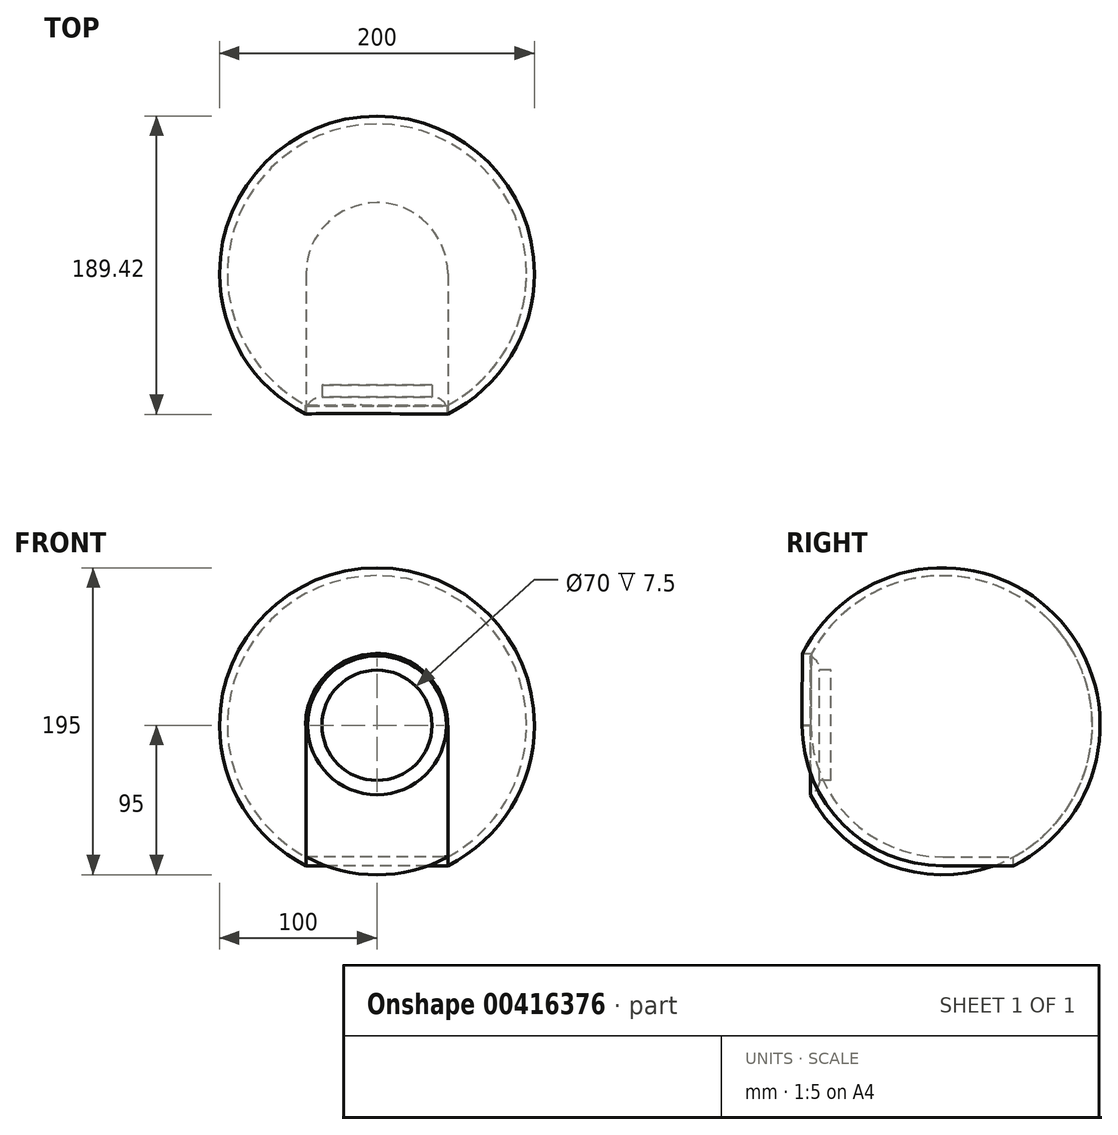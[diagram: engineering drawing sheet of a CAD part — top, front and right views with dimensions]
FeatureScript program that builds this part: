
annotation { "Feature Type Name" : "Feature", "Feature Type Description" : "" }
export const myFeature = defineFeature(function(context is Context, id is Id, definition is map)
    precondition{}
    {
        {
            assignVariable(context, id + "F0", {"name" : "bodyDiam", "anyValue" : 200});
        }
        {
            assignVariable(context, id + "F1", {"name" : "shellThickness", "anyValue" : 5});
        }
        {
            var Q0;
            Q0=qCreatedBy(makeId("Front.planeOp"),FACE);
            var sketch = newSketch(context, id + "F2", { "sketchPlane" : qUnion([Q0])});
            skCircle(sketch, "E0", {"center": v(0, 0) * mm, "radius": 100 * mm});
            skCircle(sketch, "E1", {"center": v(-0.22, 0.55) * mm, "radius": 45 * mm});
            skLineSegment(sketch, "E2", {"start": v(0, 0) * mm, "end": v(100, 0) * mm});
            skLineSegment(sketch, "E3", {"start": v(0, 0) * mm, "end": v(-100, 0) * mm});
            skCircle(sketch, "E4", {"center": v(0, 0) * mm, "radius": 95 * mm});
            skSolve(sketch);
        }
        {
            var Q0;
            Q0=qCreatedBy(makeId("Top.planeOp"),FACE);
            var sketch = newSketch(context, id + "F3", { "sketchPlane" : qUnion([Q0])});
            skCircle(sketch, "E5", {"center": v(0, 0) * mm, "radius": 45 * mm});
            skLineSegment(sketch, "E6", {"start": v(-45, 0) * mm, "end": v(-45, -100) * mm});
            skLineSegment(sketch, "E7", {"start": v(45, 0) * mm, "end": v(45, -100) * mm});
            skLineSegment(sketch, "E8", {"start": v(45, -100) * mm, "end": v(-45, -100) * mm});
            skSolve(sketch);
        }
        {
            var Q0;
            Q0=qCreatedBy(makeId("Right.planeOp"),FACE);
            var sketch = newSketch(context, id + "F4", { "sketchPlane" : qUnion([Q0])});
            skLineSegment(sketch, "E9", {"start": v(0, 0) * mm, "end": v(-95, 0) * mm});
            skCircle(sketch, "E10", {"center": v(0, 0) * mm, "radius": 95 * mm});
            skLineSegment(sketch, "E11", {"start": v(-88.32, 35) * mm, "end": v(-88.32, -35) * mm});
            skCircle(sketch, "E12", {"center": v(-88.32, -35) * mm, "radius": 10 * mm});
            skCircle(sketch, "E13", {"center": v(-88.32, 35) * mm, "radius": 10 * mm});
            skLineSegment(sketch, "E14", {"start": v(-78.32, 35) * mm, "end": v(-78.32, -35) * mm});
            skSolve(sketch);
        }
        {
            var Q0;
            {var subQ0=sQuery(id+"F2.wireOp",EDGE,"E2");var subQ1=sQuery(id+"F2.wireOp",EDGE,"E0");var subQ2=makeQuery(id+"F2.imprint","INTERSECT",VERTEX,{"derivedFrom":[subQ1,subQ0]});Q0=makeQuery(id+"F2.imprint","IMPRINT",FACE,{"disambiguationData":[TD([[makeQuery(id+"F2.imprint","IMPRINT",EDGE,{"disambiguationData":[TD([[subQ2,-1.0]])],"derivedFrom":subQ1}),1.0]])]});}
            var Q1;
            {var subQ0=sQuery(id+"F2.wireOp",EDGE,"E2");var subQ1=sQuery(id+"F2.wireOp",EDGE,"E1");var subQ2=makeQuery(id+"F2.imprint","INTERSECT",VERTEX,{"derivedFrom":[subQ1,subQ0]});Q1=makeQuery(id+"F2.imprint","IMPRINT",FACE,{"disambiguationData":[TD([[makeQuery(id+"F2.imprint","IMPRINT",EDGE,{"disambiguationData":[TD([[subQ2,-1.0]])],"derivedFrom":subQ1}),1.0]])]});}
            var Q2;
            {var subQ0=sQuery(id+"F2.wireOp",EDGE,"E2");var subQ1=sQuery(id+"F2.wireOp",EDGE,"E1");var subQ2=makeQuery(id+"F2.imprint","INTERSECT",VERTEX,{"derivedFrom":[subQ1,subQ0]});Q2=makeQuery(id+"F2.imprint","IMPRINT",FACE,{"disambiguationData":[TD([[makeQuery(id+"F2.imprint","IMPRINT",EDGE,{"disambiguationData":[TD([[subQ2,-1.0]])],"derivedFrom":subQ1}),-1.0]])]});}
            var Q3;
            Q3=sQuery(id+"F2.wireOp",EDGE,"E3");
            revolve(context, id + "F5", {"entities" : qUnion([Q0, Q1, Q2]), "axis" : qUnion([Q3]), "revolveType" : RevolveType.FULL});
        }
        {
            var Q0;
            Q0=makeQuery(id+"F5.opRevolve","SWEPT_FACE",FACE,{"disambiguationData":[OSD([sQuery(id+"F2.wireOp",EDGE,"E0")])]});
            var Q1;
            Q1=makeQuery(id+"F5.opRevolve","SWEPT_BODY",BODY,{"disambiguationData":[OSD([sQuery(id+"F2.wireOp",EDGE,"E0"),sQuery(id+"F2.wireOp",EDGE,"E2"),sQuery(id+"F2.wireOp",EDGE,"E3")])]});
            shell(context, id + "F6", {"isHollow" : true, "entities" : qUnion([Q0]), "parts" : qUnion([Q1]), "thickness" : (getVariable(context, 'shellThickness')) * mm});
        }
        {
            var Q0;
            {var subQ0=sQuery(id+"F2.wireOp",EDGE,"E2");var subQ1=sQuery(id+"F2.wireOp",EDGE,"E1");var subQ2=makeQuery(id+"F2.imprint","INTERSECT",VERTEX,{"derivedFrom":[subQ1,subQ0]});Q0=makeQuery(id+"F2.imprint","IMPRINT",FACE,{"disambiguationData":[TD([[makeQuery(id+"F2.imprint","IMPRINT",EDGE,{"disambiguationData":[TD([[subQ2,-1.0]])],"derivedFrom":subQ1}),1.0]])]});}
            extrude(context, id + "F7", {"entities" : qUnion([Q0]), "operationType" : NewBodyOperationType.REMOVE, "depth" : (getVariable(context, 'bodyDiam')) * mm});
        }
        {
            var Q0;
            {var subQ0=sQuery(id+"F3.wireOp",EDGE,"E5");var subQ1=makeQuery(id+"F3.imprint","INTERSECT",VERTEX,{"derivedFrom":[subQ0,sQuery(id+"F3.wireOp",EDGE,"E6")]});Q0=makeQuery(id+"F3.imprint","IMPRINT",FACE,{"disambiguationData":[TD([[makeQuery(id+"F3.imprint","IMPRINT",EDGE,{"disambiguationData":[TD([[subQ1,1.0]])],"derivedFrom":subQ0}),1.0]])]});}
            var Q1;
            {var subQ0=sQuery(id+"F3.wireOp",EDGE,"E6");Q1=makeQuery(id+"F3.imprint","IMPRINT",FACE,{"disambiguationData":[TD([[makeQuery(id+"F3.imprint","IMPRINT",EDGE,{"derivedFrom":subQ0}),1.0]])]});}
            extrude(context, id + "F8", {"entities" : qUnion([Q0, Q1]), "operationType" : NewBodyOperationType.REMOVE, "oppositeDirection" : true, "depth" : (getVariable(context, 'bodyDiam')) * mm});
        }
        {
            var Q0;
            {var subQ0=sQuery(id+"F2.wireOp",EDGE,"E2");var subQ1=sQuery(id+"F2.wireOp",EDGE,"E1");var subQ2=makeQuery(id+"F2.imprint","INTERSECT",VERTEX,{"derivedFrom":[subQ1,subQ0]});Q0=makeQuery(id+"F2.imprint","IMPRINT",FACE,{"disambiguationData":[TD([[makeQuery(id+"F2.imprint","IMPRINT",EDGE,{"disambiguationData":[TD([[subQ2,-1.0]])],"derivedFrom":subQ1}),-1.0]])]});}
            var Q1;
            {var subQ0=sQuery(id+"F2.wireOp",EDGE,"E2");var subQ1=sQuery(id+"F2.wireOp",EDGE,"E1");var subQ2=makeQuery(id+"F2.imprint","INTERSECT",VERTEX,{"derivedFrom":[subQ1,subQ0]});Q1=makeQuery(id+"F2.imprint","IMPRINT",FACE,{"disambiguationData":[TD([[makeQuery(id+"F2.imprint","IMPRINT",EDGE,{"disambiguationData":[TD([[subQ2,-1.0]])],"derivedFrom":subQ1}),1.0]])]});}
            var Q2;
            Q2=sQuery(id+"F2.wireOp",EDGE,"E2");
            revolve(context, id + "F9", {"entities" : qUnion([Q0, Q1]), "axis" : qUnion([Q2]), "revolveType" : RevolveType.FULL});
        }
        {
            var Q0;
            {var subQ0=sQuery(id+"F4.wireOp",EDGE,"E11");var subQ1=sQuery(id+"F4.wireOp",EDGE,"E10");var subQ2=makeQuery(id+"F4.imprint","INTERSECT",VERTEX,{"disambiguationData":[OD(0.0)],"derivedFrom":[subQ1,subQ0]});Q0=makeQuery(id+"F4.imprint","IMPRINT",FACE,{"disambiguationData":[TD([[makeQuery(id+"F4.imprint","IMPRINT",EDGE,{"disambiguationData":[TD([[subQ2,1.0]])],"derivedFrom":subQ1}),1.0]])]});}
            var Q1;
            {var subQ0=sQuery(id+"F4.wireOp",EDGE,"E11");var subQ1=sQuery(id+"F4.wireOp",EDGE,"E10");var subQ2=makeQuery(id+"F4.imprint","INTERSECT",VERTEX,{"disambiguationData":[OD(0.0)],"derivedFrom":[subQ1,subQ0]});Q1=makeQuery(id+"F4.imprint","IMPRINT",FACE,{"disambiguationData":[TD([[makeQuery(id+"F4.imprint","IMPRINT",EDGE,{"disambiguationData":[TD([[subQ2,-1.0]])],"derivedFrom":subQ1}),1.0]])]});}
            var Q2;
            {var subQ0=sQuery(id+"F4.wireOp",EDGE,"E10");var subQ1=sQuery(id+"F4.wireOp",EDGE,"E9");var subQ2=makeQuery(id+"F4.imprint","INTERSECT",VERTEX,{"derivedFrom":[subQ1,subQ0]});Q2=makeQuery(id+"F4.imprint","IMPRINT",FACE,{"disambiguationData":[TD([[makeQuery(id+"F4.imprint","IMPRINT",EDGE,{"disambiguationData":[TD([[subQ2,1.0]])],"derivedFrom":subQ1}),-1.0]])]});}
            var Q3;
            {var subQ0=sQuery(id+"F4.wireOp",EDGE,"E14");var subQ1=sQuery(id+"F4.wireOp",EDGE,"E9");var subQ2=makeQuery(id+"F4.imprint","INTERSECT",VERTEX,{"derivedFrom":[subQ1,subQ0]});Q3=makeQuery(id+"F4.imprint","IMPRINT",FACE,{"disambiguationData":[TD([[makeQuery(id+"F4.imprint","IMPRINT",EDGE,{"disambiguationData":[TD([[subQ2,-1.0]])],"derivedFrom":subQ1}),-1.0]])]});}
            var Q4;
            Q4=sQuery(id+"F4.wireOp",EDGE,"E9");
            revolve(context, id + "F10", {"operationType" : NewBodyOperationType.REMOVE, "entities" : qUnion([Q0, Q1, Q2, Q3]), "axis" : qUnion([Q4]), "revolveType" : RevolveType.FULL, "oppositeDirection" : true});
        }
        {
            var Q0;
            Q0=makeQuery(id+"F10.boolean.opBoolean","COPY",FACE,{"derivedFrom":makeQuery(id+"F10.opRevolve","SWEPT_FACE",FACE,{"disambiguationData":[OSD([sQuery(id+"F4.wireOp",EDGE,"E14")])]})});
            extrude(context, id + "F11", {"entities" : qUnion([Q0]), "operationType" : NewBodyOperationType.REMOVE, "oppositeDirection" : true, "depth" : 7.5 * mm});
        }
    });
